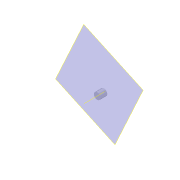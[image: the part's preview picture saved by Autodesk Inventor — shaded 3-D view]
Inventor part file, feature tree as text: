
AUTODESK INVENTOR PART (.ipt)
format: ipt  version: 2022 (Build 260153000, 153)  size: 93,184 bytes
history: native  units: mm
features: other x5, reference x3, plane x1, sketch x1, extrude x1
ambient origin geometry x8: Origin, YZ Plane, XZ Plane, XY Plane, X Axis, Y Axis, Z Axis, Center Point
bodies: Solid1 (feature_tree)
feature tree (11):
  plane  "Work Plane1"
  sketch  "Sketch1"  dims[d0=11.2mm d2=10.5mm d3=5.0mm d4=10.0mm d5=0.0mm]
  other  "Work Point1"
  extrude  "Extrusion1"  Depth=10.0mm
  other  "Arbeitsachse1"
  reference  "Reference1"
  reference  "Reference2"
  reference  "Reference3"
  other  "00_KES400.iam"
  other  "00_KES_Bluray_Magnet:1"
  other  "00_KES400_Bluray_Lens:1"
